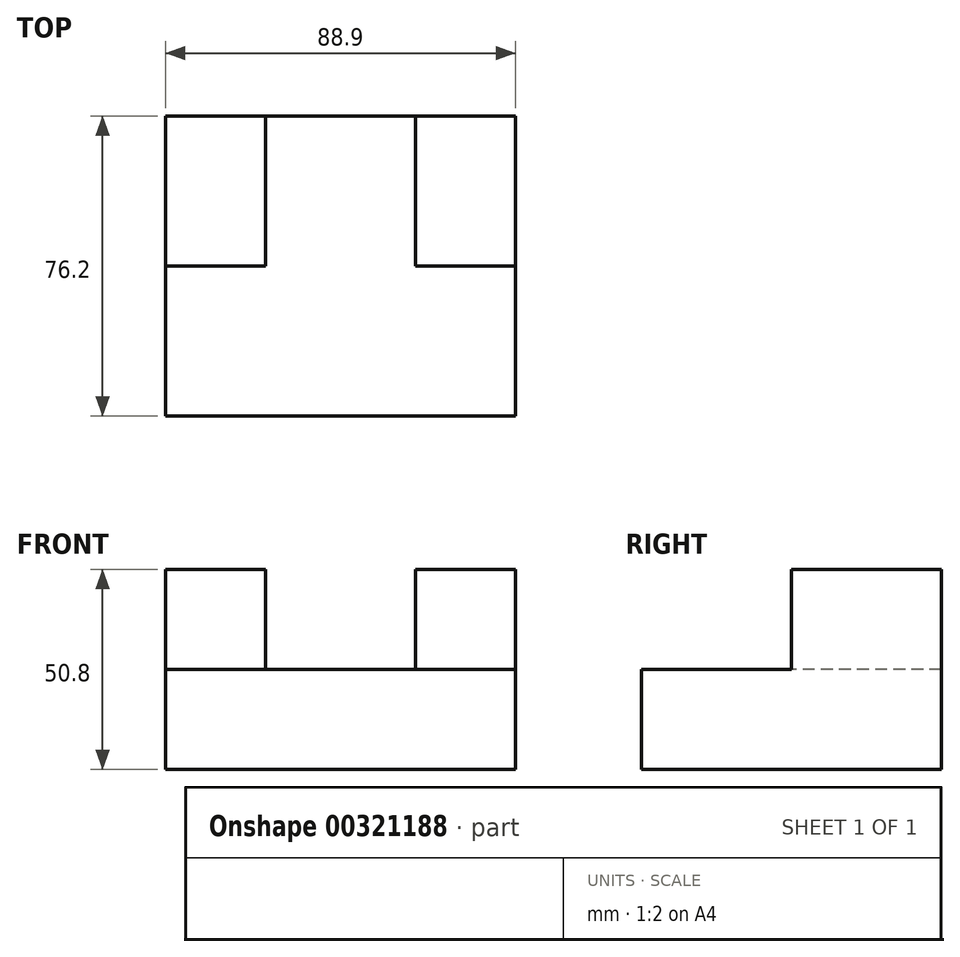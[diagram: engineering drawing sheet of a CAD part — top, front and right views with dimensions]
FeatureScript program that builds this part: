
annotation { "Feature Type Name" : "Feature", "Feature Type Description" : "" }
export const myFeature = defineFeature(function(context is Context, id is Id, definition is map)
    precondition{}
    {
        {
            var Q0;
            Q0=qCreatedBy(makeId("Right.planeOp"),FACE);
            var sketch = newSketch(context, id + "F0", { "sketchPlane" : qUnion([Q0])});
            skLineSegment(sketch, "E0", {"start": v(-39.34, -45.6) * mm, "end": v(36.86, -45.6) * mm});
            skLineSegment(sketch, "E1", {"start": v(36.86, -45.6) * mm, "end": v(36.86, 5.2) * mm});
            skLineSegment(sketch, "E2", {"start": v(36.86, 5.2) * mm, "end": v(-1.24, 5.2) * mm});
            skLineSegment(sketch, "E3", {"start": v(-1.24, 5.2) * mm, "end": v(-1.24, -20.2) * mm});
            skLineSegment(sketch, "E4", {"start": v(-1.24, -20.2) * mm, "end": v(-39.34, -20.2) * mm});
            skLineSegment(sketch, "E5", {"start": v(-39.34, -20.2) * mm, "end": v(-39.34, -45.6) * mm});
            skSolve(sketch);
        }
        {
            var Q0;
            Q0=makeQuery(id+"F0.imprint","IMPRINT",FACE,{"disambiguationData":[TD([[makeQuery(id+"F0.imprint","IMPRINT",EDGE,{"derivedFrom":sQuery(id+"F0.wireOp",EDGE,"E0")}),1.0]])]});
            extrude(context, id + "F1", {"entities" : qUnion([Q0]), "depth" : 88.9 * mm});
        }
        {
            var Q0;
            Q0=makeQuery(id+"F1.opExtrude","SWEPT_FACE",FACE,{"disambiguationData":[OSD([sQuery(id+"F0.wireOp",EDGE,"E3")])]});
            var sketch = newSketch(context, id + "F2", { "sketchPlane" : qUnion([Q0])});
            skLineSegment(sketch, "E6.bottom", {"start": v(25.4, -20.2) * mm, "end": v(63.5, -20.2) * mm});
            skLineSegment(sketch, "E6.top", {"start": v(25.4, 5.2) * mm, "end": v(63.5, 5.2) * mm});
            skLineSegment(sketch, "E6.left", {"start": v(25.4, -20.2) * mm, "end": v(25.4, 5.2) * mm});
            skLineSegment(sketch, "E6.right", {"start": v(63.5, -20.2) * mm, "end": v(63.5, 5.2) * mm});
            skSolve(sketch);
        }
        {
            var Q0;
            Q0=makeQuery(id+"F2.imprint","IMPRINT",FACE,{"disambiguationData":[TD([[makeQuery(id+"F2.imprint","IMPRINT",EDGE,{"derivedFrom":sQuery(id+"F2.wireOp",EDGE,"E6.bottom")}),-1.0]])]});
            extrude(context, id + "F3", {"entities" : qUnion([Q0]), "operationType" : NewBodyOperationType.REMOVE, "endBound" : BoundingType.THROUGH_ALL, "oppositeDirection" : true, "depth" : 25.4 * mm});
        }
    });
